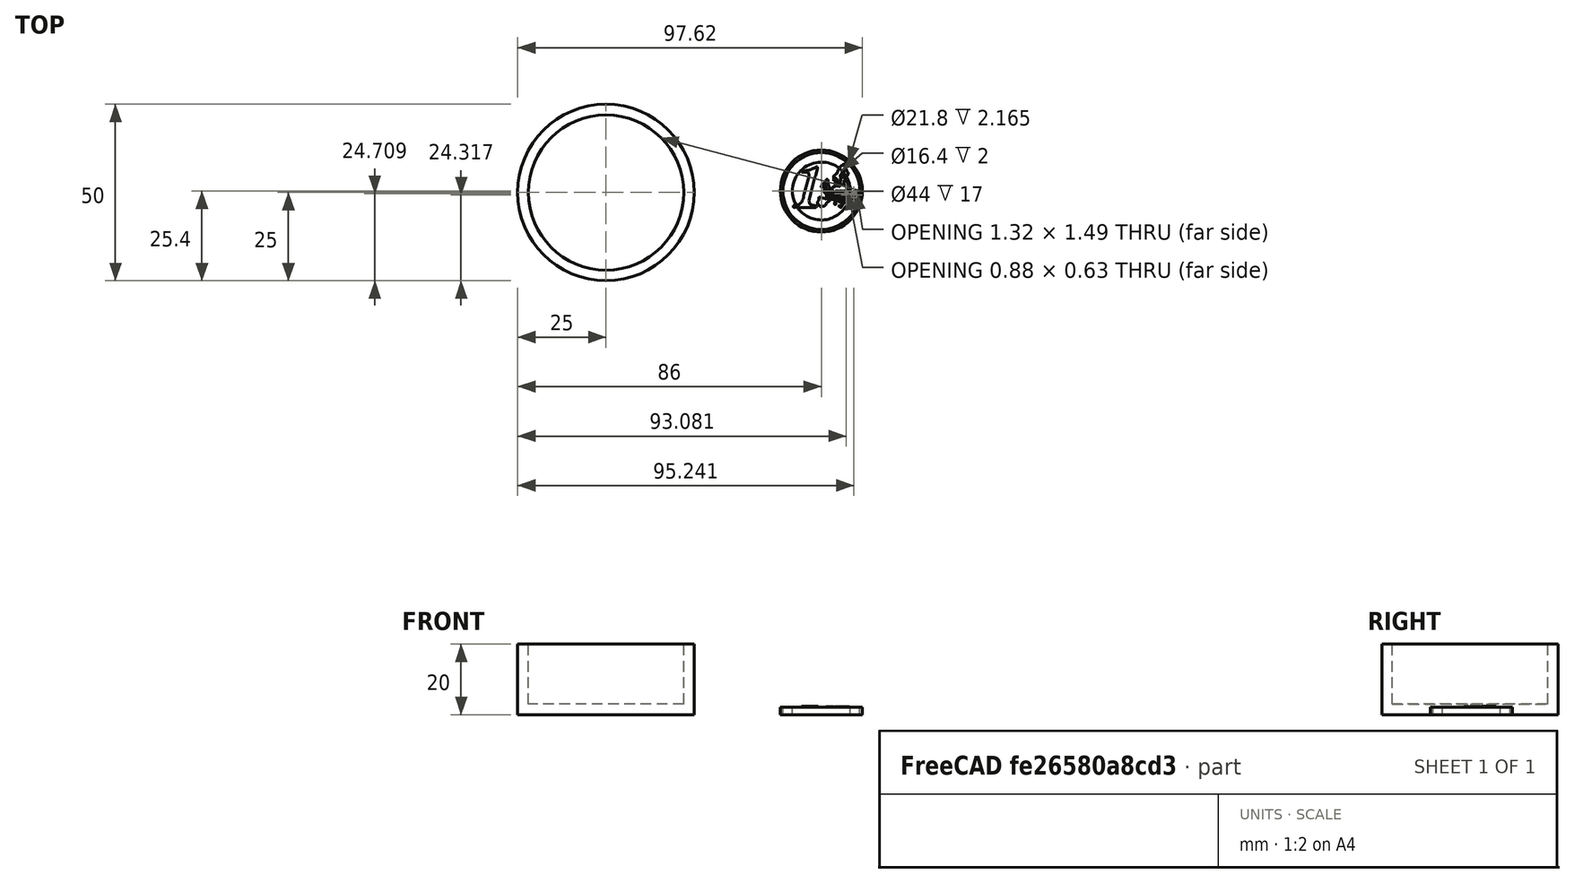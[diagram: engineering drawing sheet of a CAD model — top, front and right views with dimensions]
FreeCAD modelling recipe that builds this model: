
FCSTD DOCUMENT  (FreeCAD 0.16R6626 (Git))
Label: work
License: CreativeCommons Attribution-ShareAlike
LicenseURL: http://creativecommons.org/licenses/by-sa/4.0/
objects: Part::Cylinder×2, Part::Compound×1, Spreadsheet::Sheet×1, Part::Cut×1
note: 4 computed .brp shape members not serialized (recipe doc carries the construction recipe); baked Part::Feature solids carry a one-line shape summary decoded from their .brp

FEATURE [Part::Compound] Compound  label="Euro-coin-ready"
  Placement = pos=(61,0,0) rot=(0,0,1;0rad)
FEATURE [Spreadsheet::Sheet] Spreadsheet
  cells = B3=Diametro; C3(diametro)=50; B4=Altura; C4(altura)=20
FEATURE [Part::Cylinder] Cylinder
  Angle = 360
  Height = 20
  Radius = 25
  expr: Height = Spreadsheet.altura
  expr: Radius = Spreadsheet.diametro / 2
FEATURE [Part::Cylinder] Cylinder001
  Angle = 360
  Height = 20
  Placement = pos=(0,0,3) rot=(0,0,1;0rad)
  Radius = 22
  expr: Height = Spreadsheet.altura
  expr: Radius = Spreadsheet.diametro / 2 - 3
FEATURE [Part::Cut] Cut
  Base = -> Cylinder
  Tool = -> Cylinder001
